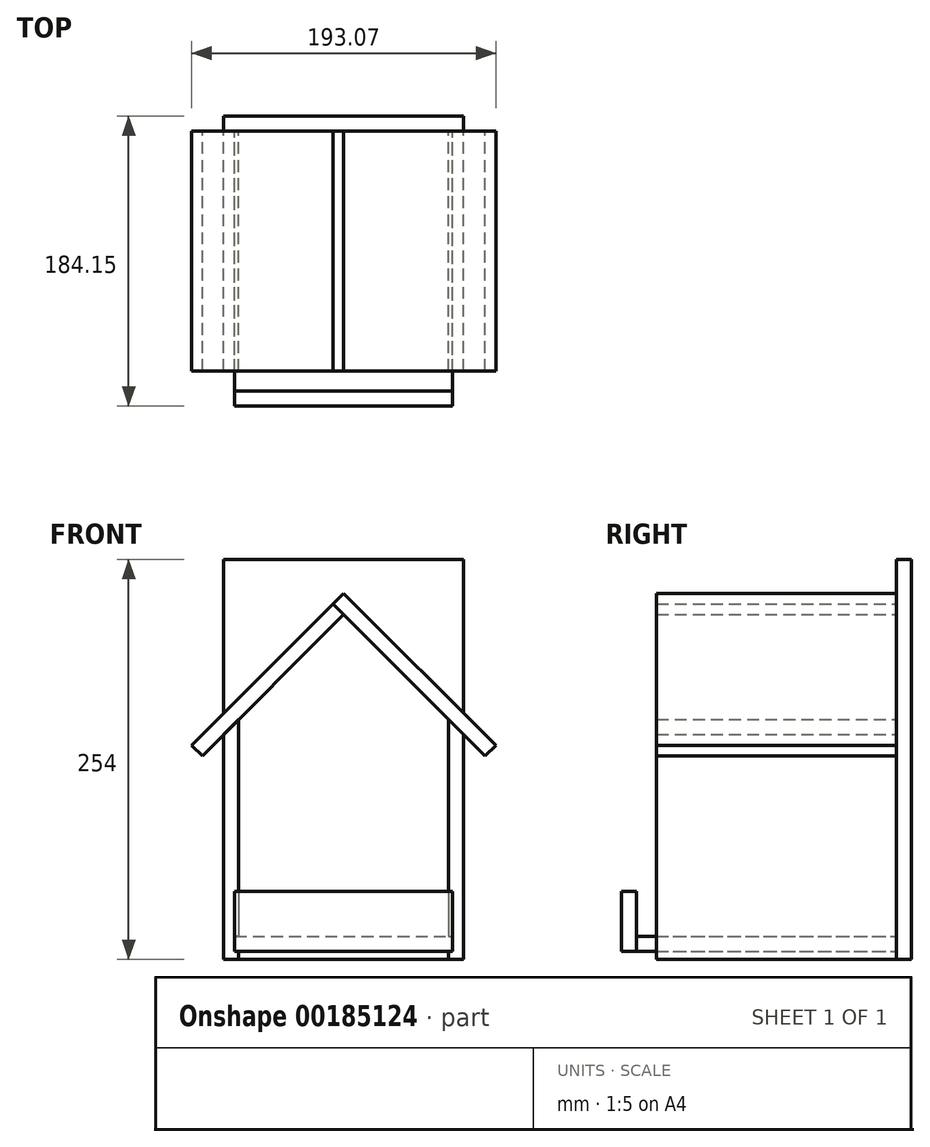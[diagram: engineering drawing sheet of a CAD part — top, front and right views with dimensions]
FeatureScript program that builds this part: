
annotation { "Feature Type Name" : "Feature", "Feature Type Description" : "" }
export const myFeature = defineFeature(function(context is Context, id is Id, definition is map)
    precondition{}
    {
        {
            var Q0;
            Q0=qCreatedBy(makeId("Front.planeOp"),FACE);
            var sketch = newSketch(context, id + "F0", { "sketchPlane" : qUnion([Q0])});
            skLineSegment(sketch, "E0.top", {"start": v(0, -152.4) * mm, "end": v(9.53, -152.4) * mm});
            skLineSegment(sketch, "E0.left", {"start": v(0, 0) * mm, "end": v(0, -137.8) * mm});
            skLineSegment(sketch, "E0.right", {"start": v(9.53, -9.52) * mm, "end": v(9.53, -152.4) * mm});
            skLineSegment(sketch, "E1", {"start": v(0, 0) * mm, "end": v(9.52, -9.52) * mm});
            skLineSegment(sketch, "E2", {"start": v(-66.67, 0) * mm, "end": v(-66.67, -157.95) * mm, "construction": true});
            skLineSegment(sketch, "E3.bottom", {"start": v(0, -137.8) * mm, "end": v(2.54, -137.8) * mm});
            skLineSegment(sketch, "E3.top", {"start": v(0, -147.32) * mm, "end": v(2.54, -147.32) * mm});
            skLineSegment(sketch, "E3.right", {"start": v(2.54, -137.8) * mm, "end": v(2.54, -147.32) * mm});
            skLineSegment(sketch, "E4.trimOffspring", {"start": v(0, -147.32) * mm, "end": v(0, -152.4) * mm});
            skLineSegment(sketch, "E5.MirrorCS", {"start": v(-133.35, -147.32) * mm, "end": v(-135.9, -147.32) * mm});
            skLineSegment(sketch, "E6.MirrorCS", {"start": v(-133.35, -147.32) * mm, "end": v(-133.35, -152.4) * mm});
            skLineSegment(sketch, "E7.MirrorCS", {"start": v(-133.35, -137.8) * mm, "end": v(-135.9, -137.8) * mm});
            skLineSegment(sketch, "E8.MirrorCS", {"start": v(-135.9, -137.8) * mm, "end": v(-135.9, -147.32) * mm});
            skLineSegment(sketch, "E9.MirrorCS", {"start": v(-133.35, 0) * mm, "end": v(-142.88, -9.53) * mm});
            skLineSegment(sketch, "E10.MirrorCS", {"start": v(-133.35, 0) * mm, "end": v(-133.35, -137.8) * mm});
            skLineSegment(sketch, "E11.MirrorCS", {"start": v(-133.35, -152.4) * mm, "end": v(-142.88, -152.4) * mm});
            skLineSegment(sketch, "E12.MirrorCS", {"start": v(-142.88, -9.53) * mm, "end": v(-142.88, -152.4) * mm});
            skSolve(sketch);
        }
        {
            var Q0;
            Q0 = qSketchRegion(id + "F0", true);
            extrude(context, id + "F1", {"entities" : qUnion([Q0]), "depth" : 152.4 * mm});
        }
        {
            var Q0;
            Q0=qCreatedBy(makeId("Front.planeOp"),FACE);
            var sketch = newSketch(context, id + "F2", { "sketchPlane" : qUnion([Q0])});
            skLineSegment(sketch, "E13.0", {"start": v(-135.9, -137.8) * mm, "end": v(-135.9, -147.32) * mm});
            skLineSegment(sketch, "E13.1", {"start": v(2.54, -137.8) * mm, "end": v(2.54, -147.32) * mm});
            skLineSegment(sketch, "E14", {"start": v(-135.9, -137.8) * mm, "end": v(2.54, -137.8) * mm});
            skLineSegment(sketch, "E15", {"start": v(-135.9, -147.32) * mm, "end": v(2.54, -147.32) * mm});
            skSolve(sketch);
        }
        {
            var Q0;
            Q0 = qSketchRegion(id + "F2", true);
            extrude(context, id + "F3", {"entities" : qUnion([Q0]), "depth" : 165.1 * mm});
        }
        {
            var Q0;
            Q0=qCreatedBy(makeId("Front.planeOp"),FACE);
            var sketch = newSketch(context, id + "F4", { "sketchPlane" : qUnion([Q0])});
            skLineSegment(sketch, "E16.0", {"start": v(-135.9, -137.8) * mm, "end": v(2.54, -137.8) * mm});
            skLineSegment(sketch, "E17", {"start": v(-66.68, -137.8) * mm, "end": v(-66.68, 99.2) * mm, "construction": true});
            skLineSegment(sketch, "E18", {"start": v(-156.48, -23.13) * mm, "end": v(-66.68, 66.67) * mm});
            skPoint(sketch, "E19.orphan", {"position": v(-142.88, -9.53) * mm});
            skLineSegment(sketch, "E20.0", {"start": v(-163.21, -16.4) * mm, "end": v(-73.41, 73.41) * mm});
            skLineSegment(sketch, "E21", {"start": v(-163.21, -16.4) * mm, "end": v(-156.48, -23.13) * mm});
            skLineSegment(sketch, "E22", {"start": v(-73.41, 73.41) * mm, "end": v(-66.68, 66.67) * mm});
            skSolve(sketch);
        }
        {
            var Q0;
            Q0 = qSketchRegion(id + "F4", true);
            extrude(context, id + "F5", {"entities" : qUnion([Q0]), "depth" : 152.4 * mm});
        }
        {
            var Q0;
            Q0=qCreatedBy(makeId("Front.planeOp"),FACE);
            var sketch = newSketch(context, id + "F6", { "sketchPlane" : qUnion([Q0])});
            skPoint(sketch, "E23.0", {"position": v(-73.41, 73.41) * mm});
            skLineSegment(sketch, "E24", {"start": v(-73.41, 73.41) * mm, "end": v(23.13, -23.13) * mm});
            skLineSegment(sketch, "E25.0", {"start": v(-66.68, 80.15) * mm, "end": v(29.86, -16.4) * mm});
            skLineSegment(sketch, "E26", {"start": v(-66.68, 80.15) * mm, "end": v(-73.41, 73.41) * mm});
            skLineSegment(sketch, "E27", {"start": v(29.86, -16.4) * mm, "end": v(23.13, -23.13) * mm});
            skSolve(sketch);
        }
        {
            var Q0;
            Q0 = qSketchRegion(id + "F6", true);
            extrude(context, id + "F7", {"entities" : qUnion([Q0]), "depth" : 152.4 * mm});
        }
        {
            var Q0;
            Q0=makeQuery(id+"F3.opExtrude","CAP_FACE",FACE,{"disambiguationData":[OSD([sQuery(id+"F2.wireOp",EDGE,"E13.0"),sQuery(id+"F2.wireOp",EDGE,"E13.1"),sQuery(id+"F2.wireOp",EDGE,"E14"),sQuery(id+"F2.wireOp",EDGE,"E15")])],"isStart":false});
            var sketch = newSketch(context, id + "F8", { "sketchPlane" : qUnion([Q0])});
            skPoint(sketch, "E28.0", {"position": v(-135.9, -147.32) * mm});
            skPoint(sketch, "E29.0", {"position": v(2.54, -147.32) * mm});
            skLineSegment(sketch, "E30.bottom", {"start": v(-135.9, -147.32) * mm, "end": v(2.54, -147.32) * mm});
            skLineSegment(sketch, "E30.top", {"start": v(-135.9, -109.22) * mm, "end": v(2.54, -109.22) * mm});
            skLineSegment(sketch, "E30.left", {"start": v(-135.9, -147.32) * mm, "end": v(-135.9, -109.22) * mm});
            skLineSegment(sketch, "E30.right", {"start": v(2.54, -147.32) * mm, "end": v(2.54, -109.22) * mm});
            skSolve(sketch);
        }
        {
            var Q0;
            Q0 = qSketchRegion(id + "F8", true);
            extrude(context, id + "F9", {"entities" : qUnion([Q0]), "depth" : 9.52 * mm});
        }
        {
            var Q0;
            Q0=qCreatedBy(makeId("Front.planeOp"),FACE);
            var sketch = newSketch(context, id + "F10", { "sketchPlane" : qUnion([Q0])});
            skPoint(sketch, "E31.0", {"position": v(-142.88, -152.4) * mm});
            skPoint(sketch, "E32.0", {"position": v(9.53, -152.4) * mm});
            skLineSegment(sketch, "E33.bottom", {"start": v(-142.88, -152.4) * mm, "end": v(9.53, -152.4) * mm});
            skLineSegment(sketch, "E33.top", {"start": v(-142.88, 101.6) * mm, "end": v(9.52, 101.6) * mm});
            skLineSegment(sketch, "E33.left", {"start": v(-142.88, -152.4) * mm, "end": v(-142.88, 101.6) * mm});
            skLineSegment(sketch, "E33.right", {"start": v(9.53, -152.4) * mm, "end": v(9.53, 101.6) * mm});
            skSolve(sketch);
        }
        {
            var Q0;
            Q0 = qSketchRegion(id + "F10", true);
            extrude(context, id + "F11", {"entities" : qUnion([Q0]), "oppositeDirection" : true, "depth" : 9.52 * mm});
        }
    });
